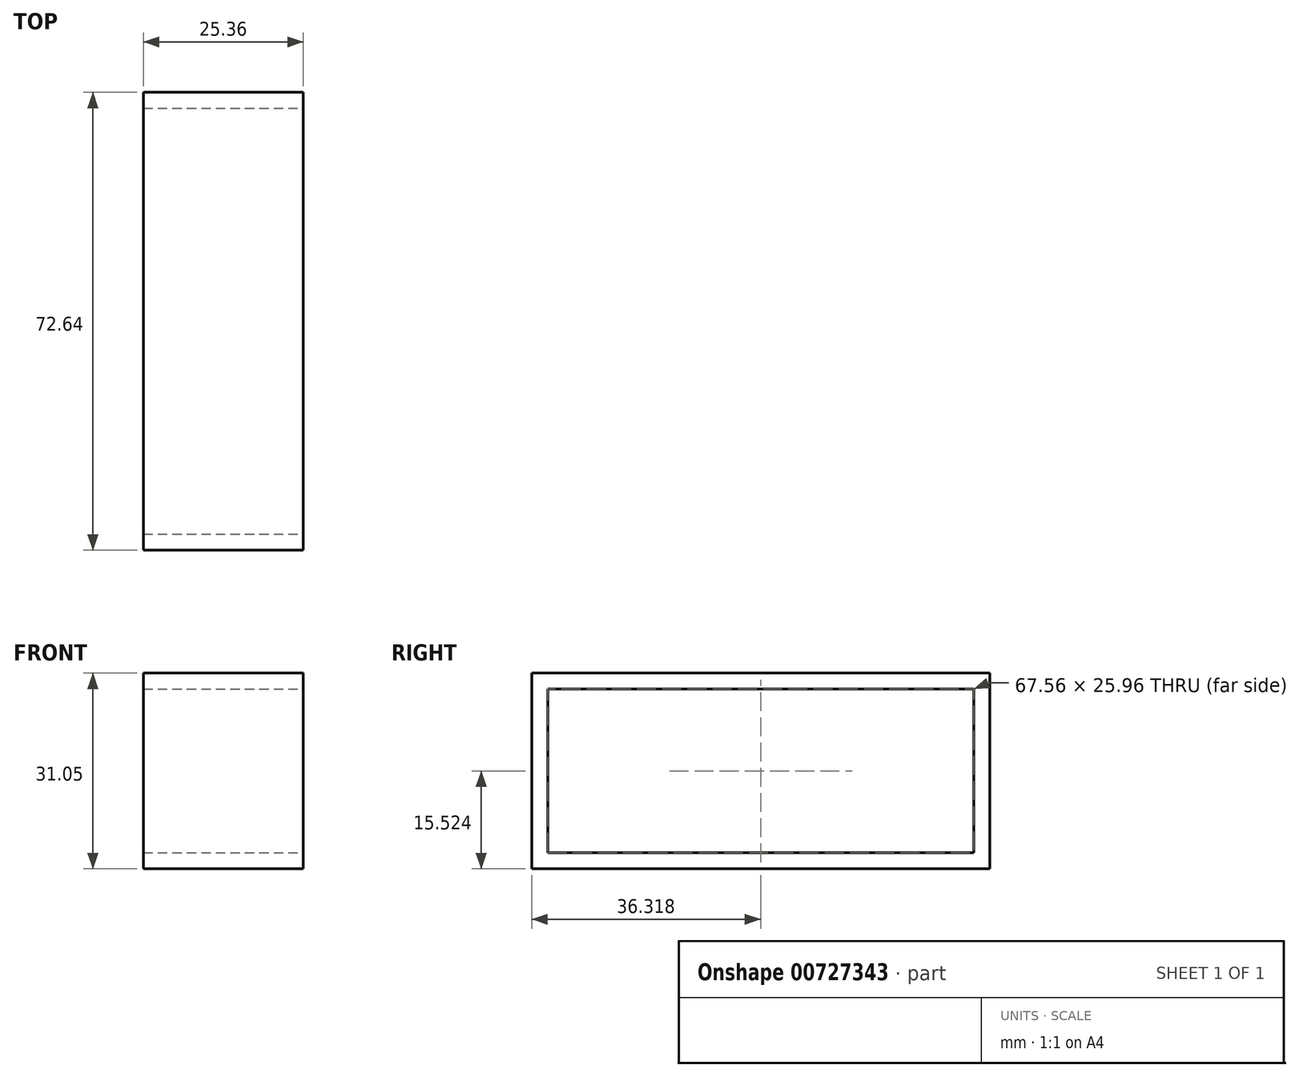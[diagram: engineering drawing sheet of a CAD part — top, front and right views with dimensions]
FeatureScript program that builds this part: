
annotation { "Feature Type Name" : "Feature", "Feature Type Description" : "" }
export const myFeature = defineFeature(function(context is Context, id is Id, definition is map)
    precondition{}
    {
        {
            var Q0;
            Q0=qCreatedBy(makeId("Front.planeOp"),FACE);
            var sketch = newSketch(context, id + "F0", { "sketchPlane" : qUnion([Q0])});
            skLineSegment(sketch, "E0.bottom", {"start": v(-43.87, 25.87) * mm, "end": v(-18.51, 25.87) * mm});
            skLineSegment(sketch, "E0.top", {"start": v(-43.87, -5.18) * mm, "end": v(-18.51, -5.18) * mm});
            skLineSegment(sketch, "E0.left", {"start": v(-43.87, 25.87) * mm, "end": v(-43.87, -5.18) * mm});
            skLineSegment(sketch, "E0.right", {"start": v(-18.51, 25.87) * mm, "end": v(-18.51, -5.18) * mm});
            skSolve(sketch);
        }
        {
            var Q0;
            Q0 = qSketchRegion(id + "F0", true);
            extrude(context, id + "F1", {"entities" : qUnion([Q0]), "depth" : 72.64 * mm, "offsetDistance" : 25.4 * mm});
        }
        {
            var Q0;
            Q0=makeQuery(id+"F1.opExtrude","SWEPT_FACE",FACE,{"disambiguationData":[OSD([sQuery(id+"F0.wireOp",EDGE,"E0.right")])]});
            var Q1;
            Q1=makeQuery(id+"F1.opExtrude","SWEPT_FACE",FACE,{"disambiguationData":[OSD([sQuery(id+"F0.wireOp",EDGE,"E0.left")])]});
            shell(context, id + "F2", {"entities" : qUnion([Q0, Q1]), "thickness" : 2.54 * mm});
        }
    });
